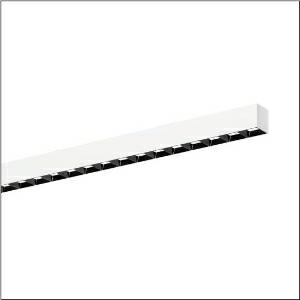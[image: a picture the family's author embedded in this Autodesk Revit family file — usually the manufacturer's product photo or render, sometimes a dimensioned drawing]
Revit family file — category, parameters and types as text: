
# Revit family: silica_21_51mx22dc3awb
name_source: partatom
category: Lighting Fixtures
units: mm (PartAtom-declared; Revit-internal decimal feet)

## family parameters
Cut with Voids When Loaded = No
Host = Face
Light Source = No
Part Type = Normal
Room Calculation Point = No
Round Connector Dimension = Use Diameter
Shared = No

## types (1)
- --- (1 x LED, 10800 lm, 69.2 W, 3000K)
    Apparent Load = 69 VA
    CIE Flux Codes = 86 100 100 100 100
    Color Rendering = 80
    Color Temperature = 3000K
    Default Elevation = 1800 mm
    Description = Silica 21, office luminaire, primary light control with darklight reflector, of PMMA, black, CAT 2 (L<= 3000cd/m²), light emission: direct distribution, primary light characteristic: symmetric, installation type: surface-mounted, LED, rated luminous flux: 10.800lm, luminous efficacy: 156lm/W, light colour: 830, colour temperature: 3000K, control gear: DALI 2, with terminal, 3+2-pole, max. 2.5mm², mains connection: 220..240V, AC, 50/60Hz, rated input power: 69.2W, luminaire housing, of aluminium, traffic white (RAL 9016), length: 3.004mm, width: 53mm, height: 53mm, protection rating (complete): IP20, insulation class (complete): insulation class I (protective earthing), certification: CE, permissible operating ambient temperature: 0..+35°C, standard: EN 50419, packaging unit: 1 piece
    Height = 53 mm
    Lamp = 1 x LED
    Lamp Light Flux = 10800 lm
    Lamp Power = 69.2 W
    Lamp count = 1
    Length = 3004 mm
    Luminous efficacy = 156 lm/W
    Manufacturer = Siteco
    ModVariant = No
    Model = 51MX22DC3AWB
    Mounting Place = Ceiling
    Mounting Type = Surface mounted
    Number of Poles = 1
    OnlyDefault = Yes
    Power Factor = 1
    Product Name = Silica 21
    Product group = office luminaire | ceiling mounted
    ProductGroupID = 301
    Protection Class = Protection class I
    Protection Degree = IP 20
    RLX_Detail_Level = 1
    RLX_Emergency_Light_Flux = 0 lm
    RLX_Emergency_Type = 0
    RLX_Emergency_Type_DB = No
    RlxData = <blob elided: 61585 chars, md5=9bc2f386>
    Socket = socket
    Standby Power = 0 W
    System Light Flux = 10800 lm
    System Power = 69 W
    Type Comments = factory setting: luminous flux: 100 % | dim-lin: 254 | 392 mA
    Type Image = l_1335873.jpg
    URL = http://relux.com
    VarID = @adj_125007
    Voltage = 0 V
    Weight = 0.00 kg
    Width = 53 mm

## geometry (parser evidence)
native form markers: Blend x4, Sweep x11
no freeform markers — native parametric forms only
